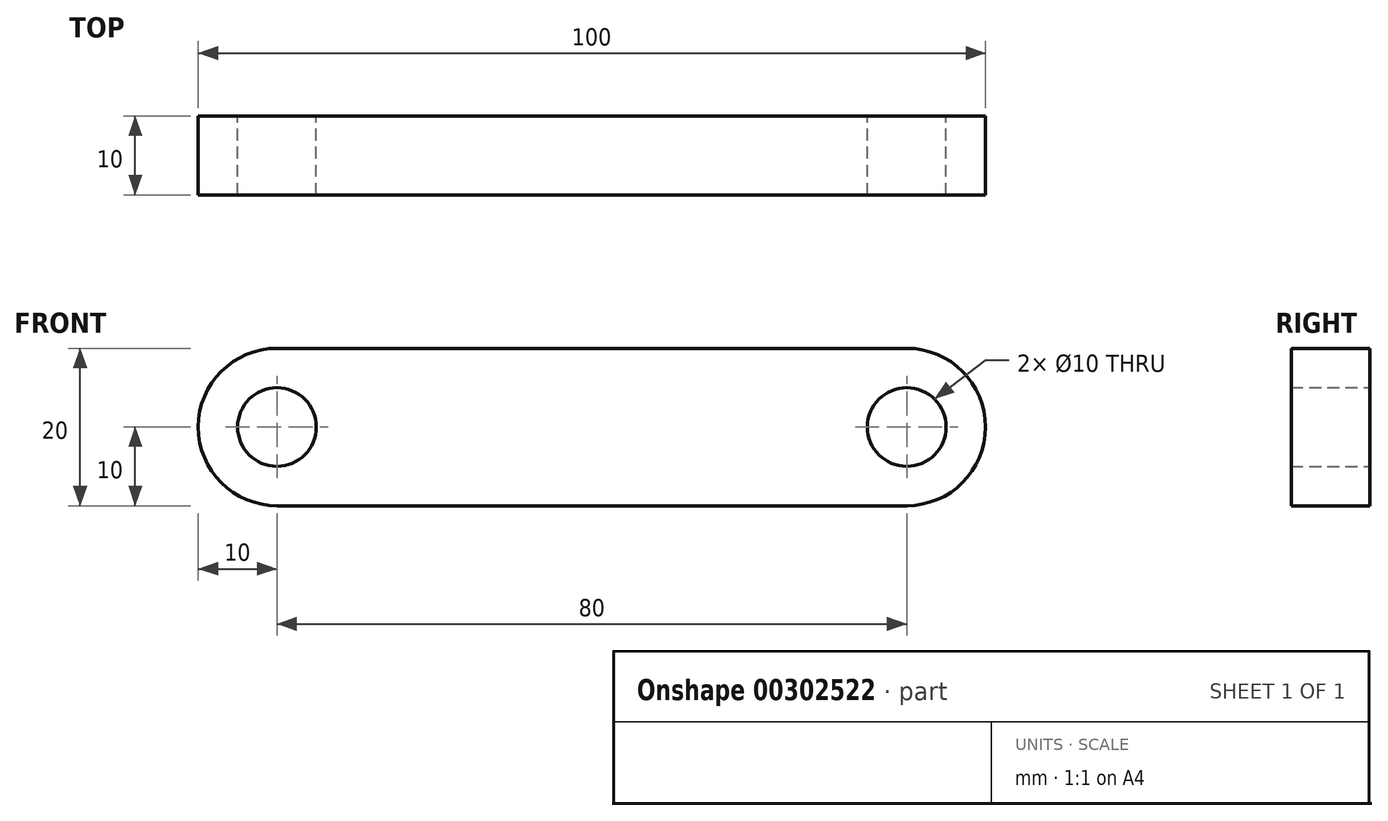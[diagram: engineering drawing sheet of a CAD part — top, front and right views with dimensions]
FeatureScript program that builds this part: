
annotation { "Feature Type Name" : "Feature", "Feature Type Description" : "" }
export const myFeature = defineFeature(function(context is Context, id is Id, definition is map)
    precondition{}
    {
        {
            var Q0;
            Q0=qCreatedBy(makeId("Front.planeOp"),FACE);
            var sketch = newSketch(context, id + "F0", { "sketchPlane" : qUnion([Q0])});
            skArc(sketch, "E0", {"start": v(0, 10) * mm, "mid": v(-10, 0) * mm, "end": v(0, -10) * mm});
            skArc(sketch, "E1", {"start": v(80, -10) * mm, "mid": v(90, 0) * mm, "end": v(80, 10) * mm});
            skLineSegment(sketch, "E2", {"start": v(80, 10) * mm, "end": v(0, 10) * mm});
            skLineSegment(sketch, "E3", {"start": v(0, -10) * mm, "end": v(80, -10) * mm});
            skCircle(sketch, "E4", {"center": v(0, 0) * mm, "radius": 5 * mm});
            skCircle(sketch, "E5", {"center": v(80, 0) * mm, "radius": 5 * mm});
            skSolve(sketch);
        }
        {
            var Q0;
            Q0=makeQuery(id+"F0.imprint","IMPRINT",FACE,{"disambiguationData":[TD([[makeQuery(id+"F0.imprint","IMPRINT",EDGE,{"derivedFrom":sQuery(id+"F0.wireOp",EDGE,"E0")}),1.0]])]});
            extrude(context, id + "F1", {"entities" : qUnion([Q0]), "depth" : 10 * mm});
        }
    });
